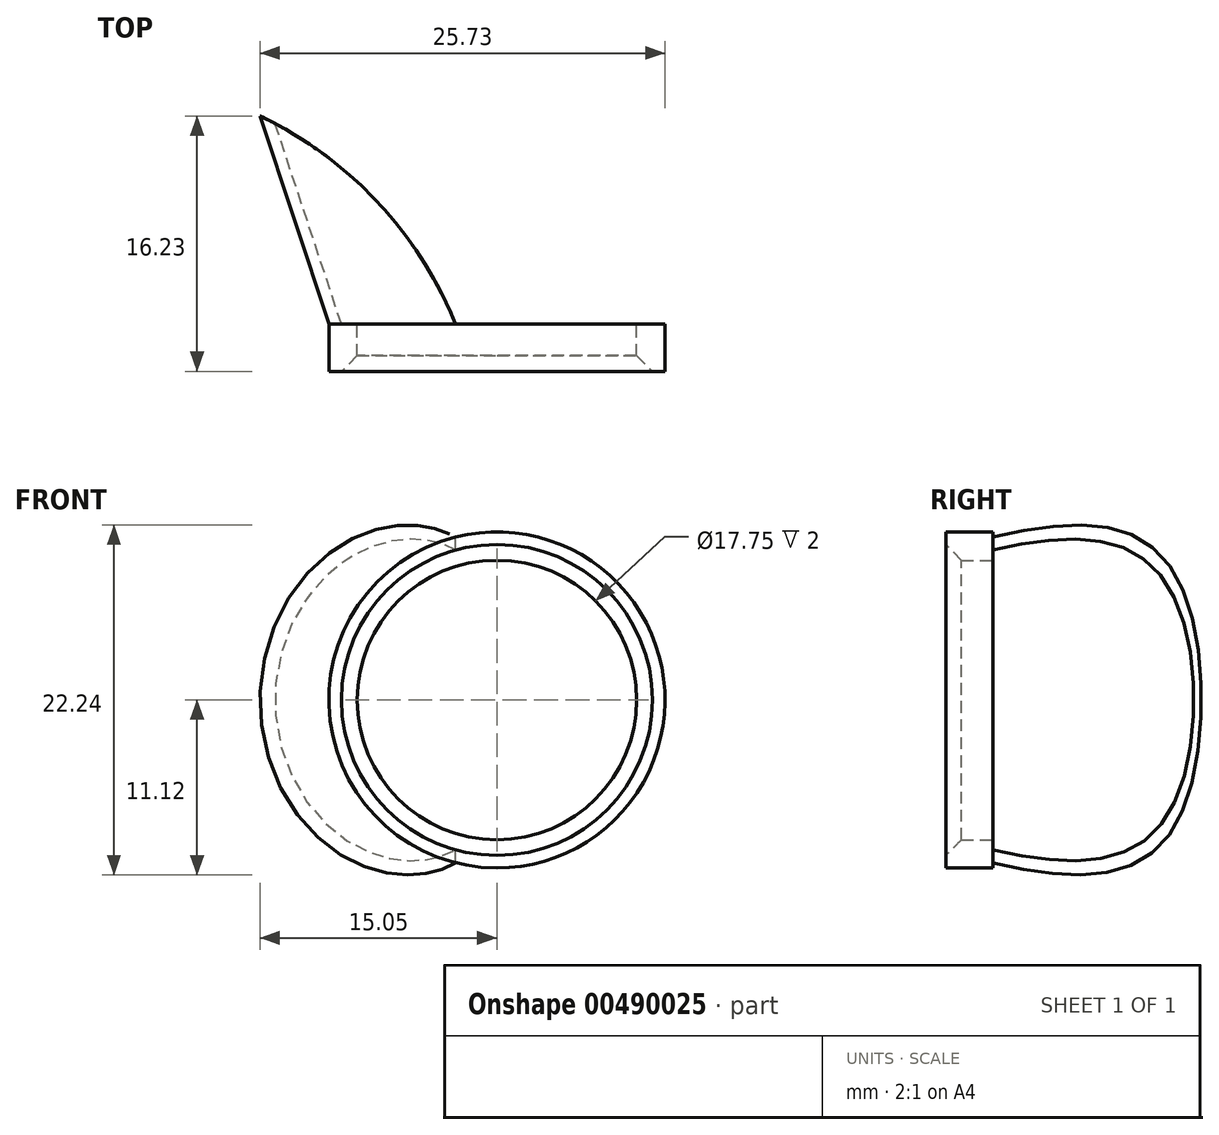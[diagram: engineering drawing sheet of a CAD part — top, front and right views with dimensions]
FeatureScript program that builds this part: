
annotation { "Feature Type Name" : "Feature", "Feature Type Description" : "" }
export const myFeature = defineFeature(function(context is Context, id is Id, definition is map)
    precondition{}
    {
        {
            var Q0;
            Q0=qCreatedBy(makeId("Front.planeOp"),FACE);
            var sketch = newSketch(context, id + "F0", { "sketchPlane" : qUnion([Q0])});
            skCircle(sketch, "E0", {"center": v(0, 0) * mm, "radius": 8.88 * mm});
            skCircle(sketch, "E1.0", {"center": v(0, 0) * mm, "radius": 10.68 * mm});
            skSolve(sketch);
        }
        {
            var Q0;
            Q0=makeQuery(id+"F0.imprint","IMPRINT",FACE,{"disambiguationData":[TD([[makeQuery(id+"F0.imprint","IMPRINT",EDGE,{"derivedFrom":sQuery(id+"F0.wireOp",EDGE,"E0")}),-1.0]])]});
            extrude(context, id + "F1", {"entities" : qUnion([Q0]), "depth" : 3 * mm});
        }
        {
            var Q0;
            Q0=qCreatedBy(makeId("Top.planeOp"),FACE);
            var sketch = newSketch(context, id + "F2", { "sketchPlane" : qUnion([Q0])});
            skLineSegment(sketch, "E2", {"start": v(-10.67, 0) * mm, "end": v(-15.15, 13.53) * mm});
            skLineSegment(sketch, "E3", {"start": v(-15.15, 13.53) * mm, "end": v(-14.35, 13.53) * mm});
            skLineSegment(sketch, "E4", {"start": v(-14.35, 13.53) * mm, "end": v(-9.87, 0) * mm});
            skLineSegment(sketch, "E5", {"start": v(-9.87, 0) * mm, "end": v(-10.67, 0) * mm});
            skSolve(sketch);
        }
        {
            var Q0;
            Q0=makeQuery(id+"F2.imprint","IMPRINT",FACE,{"disambiguationData":[TD([[makeQuery(id+"F2.imprint","IMPRINT",EDGE,{"derivedFrom":sQuery(id+"F2.wireOp",EDGE,"E2")}),-1.0]])]});
            var Q1;
            Q1=makeQuery(id+"F1.opExtrude","CAP_EDGE",EDGE,{"disambiguationData":[OSD([sQuery(id+"F0.wireOp",EDGE,"E0")])],"isStart":true});
            revolve(context, id + "F3", {"operationType" : NewBodyOperationType.ADD, "entities" : qUnion([Q0]), "axis" : qUnion([Q1]), "revolveType" : RevolveType.FULL});
        }
        {
            var Q0;
            Q0=qCreatedBy(makeId("Top.planeOp"),FACE);
            var sketch = newSketch(context, id + "F4", { "sketchPlane" : qUnion([Q0])});
            skArc(sketch, "E6", {"start": v(-2.62, 0) * mm, "mid": v(-10.55, 10.45) * mm, "end": v(-22.65, 15.5) * mm});
            skLineSegment(sketch, "E7", {"start": v(-22.65, 15.5) * mm, "end": v(-22.65, 18) * mm});
            skLineSegment(sketch, "E8", {"start": v(-22.65, 18) * mm, "end": v(26.28, 18) * mm});
            skLineSegment(sketch, "E9", {"start": v(26.28, 18) * mm, "end": v(26.28, 0) * mm});
            skLineSegment(sketch, "E10", {"start": v(26.28, 0) * mm, "end": v(-2.62, 0) * mm});
            skSolve(sketch);
        }
        {
            var Q0;
            Q0 = qSketchRegion(id + "F4", true);
            extrude(context, id + "F5", {"entities" : qUnion([Q0]), "operationType" : NewBodyOperationType.REMOVE, "oppositeDirection" : true, "depth" : 25 * mm, "hasSecondDirection" : true, "secondDirectionOppositeDirection" : false, "secondDirectionDepth" : 25 * mm});
        }
        {
            var Q0;
            Q0=makeQuery(id+"F1.opExtrude","CAP_EDGE",EDGE,{"disambiguationData":[OSD([sQuery(id+"F0.wireOp",EDGE,"E0")])],"isStart":true});
            var Q1;
            Q1=makeQuery(id+"F1.opExtrude","CAP_EDGE",EDGE,{"disambiguationData":[OSD([sQuery(id+"F0.wireOp",EDGE,"E0")])],"isStart":false});
            chamfer(context, id + "F6", {"entities" : qUnion([Q0, Q1]), "width" : 1 * mm, "tangentPropagation" : true});
        }
    });
